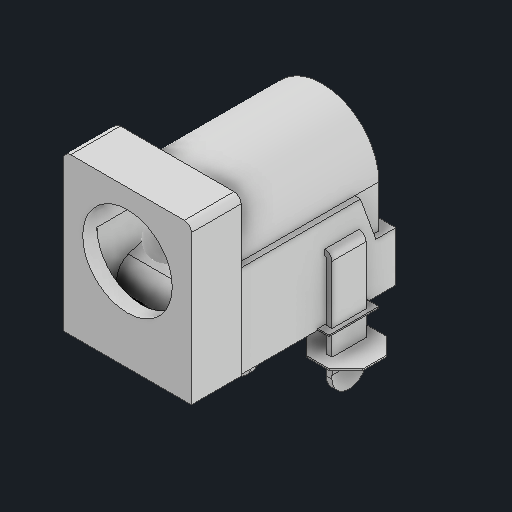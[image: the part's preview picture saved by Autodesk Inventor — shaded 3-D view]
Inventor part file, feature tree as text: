
AUTODESK INVENTOR PART (.ipt)
format: ipt  version: 2023 (Build 270158000, 158)  size: 250,880 bytes
history: native  units: in
note: dims shown in document units (in); Inventor stores cm internally (conversion verified against a paired STEP export)
features: revolve x1, fillet x1
ambient origin geometry x8: Origin, YZ Plane, XZ Plane, XY Plane, X Axis, Y Axis, Z Axis, Center Point
bodies: Solid1 (feature_tree), Solid2 (feature_tree)
feature tree (2):
  revolve  "Revolve1"  [1 undecoded]
  fillet  "Fillet5"  [1 undecoded]
note: 2 required parameter values undecoded (feature->parameter linkage not recoverable at this tier; creation-order binding heuristic only, values carry confidence <= 0.55)
